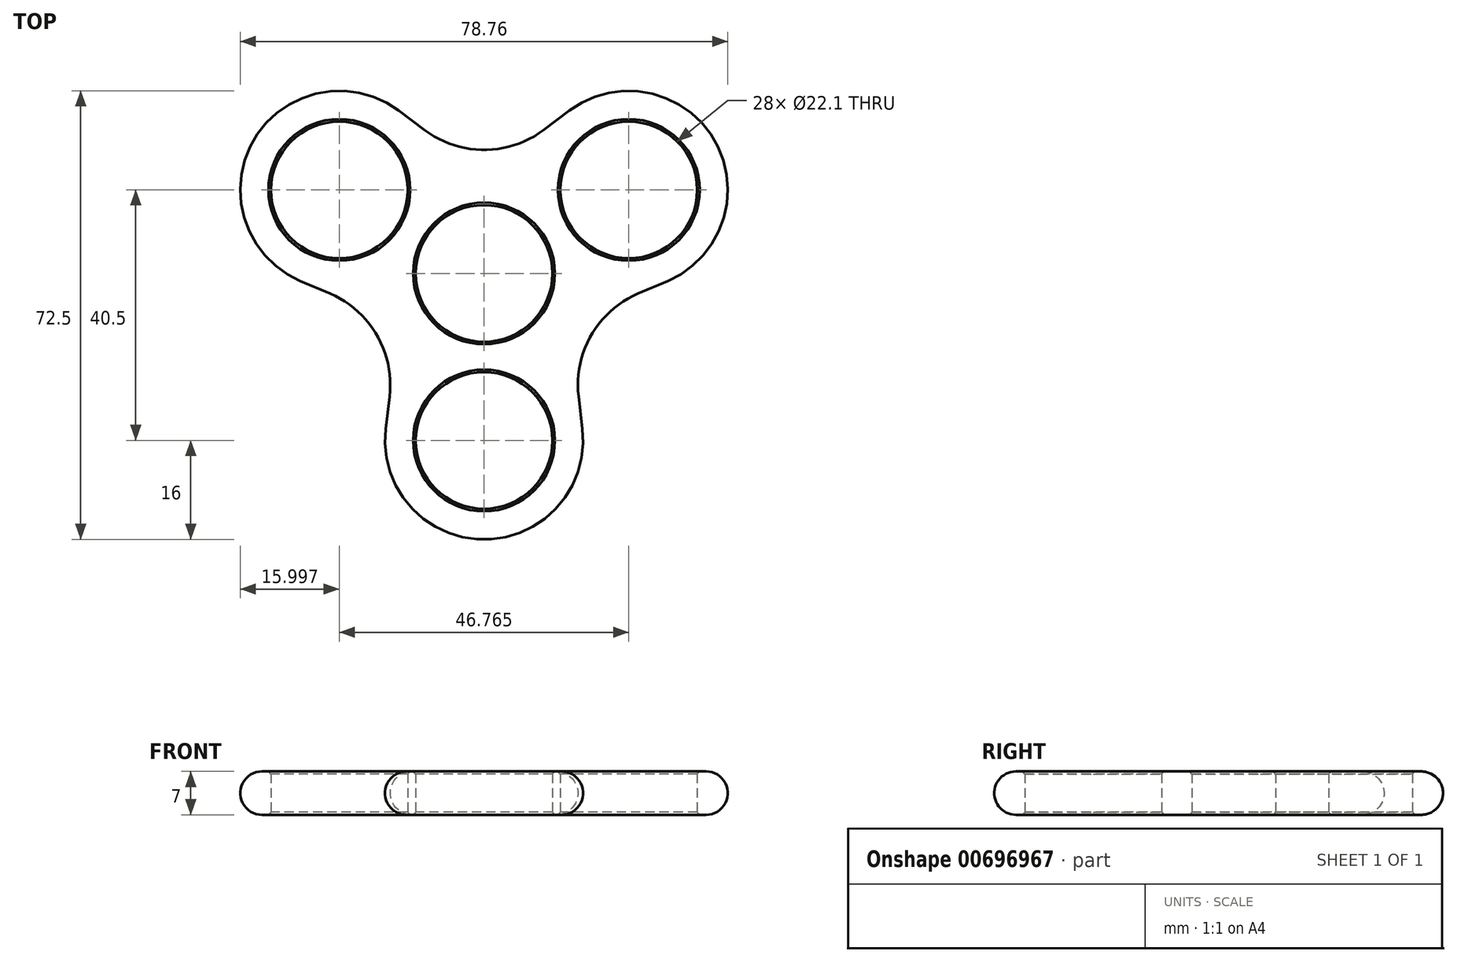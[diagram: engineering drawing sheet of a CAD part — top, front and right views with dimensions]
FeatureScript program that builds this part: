
annotation { "Feature Type Name" : "Feature", "Feature Type Description" : "" }
export const myFeature = defineFeature(function(context is Context, id is Id, definition is map)
    precondition{}
    {
        {
            var Q0;
            Q0=qCreatedBy(makeId("Top.planeOp"),FACE);
            var sketch = newSketch(context, id + "F0", { "sketchPlane" : qUnion([Q0])});
            skLineSegment(sketch, "E0", {"start": v(0, 0) * mm, "end": v(0, -27) * mm, "construction": true});
            skLineSegment(sketch, "E1", {"start": v(0, 0) * mm, "end": v(23.38, 13.5) * mm, "construction": true});
            skLineSegment(sketch, "E2", {"start": v(0, 0) * mm, "end": v(-23.38, 13.5) * mm, "construction": true});
            skCircle(sketch, "E3", {"center": v(-23.38, 13.5) * mm, "radius": 11.05 * mm});
            skCircle(sketch, "E4", {"center": v(23.38, 13.5) * mm, "radius": 11.05 * mm});
            skCircle(sketch, "E5", {"center": v(0, -27) * mm, "radius": 11.05 * mm});
            skCircle(sketch, "E6", {"center": v(0, 0) * mm, "radius": 11.05 * mm});
            skArc(sketch, "E7", {"start": v(-13.8, 26.32) * mm, "mid": v(-37.24, 21.5) * mm, "end": v(-29.7, -1.2) * mm});
            skLineSegment(sketch, "E8", {"start": v(-9.58, 23.16) * mm, "end": v(-13.8, 26.32) * mm});
            skLineSegment(sketch, "E9", {"start": v(9.58, 23.16) * mm, "end": v(13.8, 26.32) * mm});
            skPoint(sketch, "E10.visualSharp", {"position": v(0, 16) * mm});
            skArc(sketch, "E10.filletArc", {"start": v(-9.58, 23.16) * mm, "mid": v(0, 19.97) * mm, "end": v(9.58, 23.16) * mm});
            skLineSegment(sketch, "E11", {"start": v(0, 0) * mm, "end": v(-43.3, -25) * mm, "construction": true});
            skLineSegment(sketch, "E12", {"start": v(0, 0) * mm, "end": v(43.3, -25) * mm, "construction": true});
            skLineSegment(sketch, "E13", {"start": v(15.27, -19.87) * mm, "end": v(15.89, -25.11) * mm});
            skLineSegment(sketch, "E14", {"start": v(-15.27, -19.87) * mm, "end": v(-15.89, -25.11) * mm});
            skLineSegment(sketch, "E15", {"start": v(-24.84, -3.28) * mm, "end": v(-29.7, -1.2) * mm});
            skLineSegment(sketch, "E16", {"start": v(24.84, -3.28) * mm, "end": v(29.7, -1.2) * mm});
            skPoint(sketch, "E17.visualSharp", {"position": v(13.86, -8) * mm});
            skArc(sketch, "E17.filletArc", {"start": v(24.84, -3.28) * mm, "mid": v(17.3, -9.99) * mm, "end": v(15.27, -19.87) * mm});
            skPoint(sketch, "E18.visualSharp", {"position": v(-13.86, -8) * mm});
            skArc(sketch, "E18.filletArc", {"start": v(-15.27, -19.87) * mm, "mid": v(-17.3, -9.99) * mm, "end": v(-24.84, -3.28) * mm});
            skArc(sketch, "E19.trimOffspring", {"start": v(29.7, -1.2) * mm, "mid": v(37.24, 21.5) * mm, "end": v(13.8, 26.32) * mm});
            skArc(sketch, "E20.trimOffspring", {"start": v(-15.89, -25.11) * mm, "mid": v(0, -43) * mm, "end": v(15.89, -25.11) * mm});
            skSolve(sketch);
        }
        {
            var Q0;
            Q0=qSketchRegion(id+"F0",true);
            extrude(context, id + "F1", {"entities" : qUnion([Q0]), "depth" : 7 * mm, "offsetDistance" : 25 * mm});
        }
        {
            var Q0;
            Q0=makeQuery(id+"F1.opExtrude","CAP_EDGE",EDGE,{"disambiguationData":[OSD([sQuery(id+"F0.wireOp",EDGE,"E6")])],"isStart":false});
            var Q1;
            Q1=makeQuery(id+"F1.opExtrude","CAP_EDGE",EDGE,{"disambiguationData":[OSD([sQuery(id+"F0.wireOp",EDGE,"E6")])],"isStart":true});
            var Q2;
            Q2=makeQuery(id+"F1.opExtrude","CAP_EDGE",EDGE,{"disambiguationData":[OSD([sQuery(id+"F0.wireOp",EDGE,"E5")])],"isStart":false});
            var Q3;
            Q3=makeQuery(id+"F1.opExtrude","CAP_EDGE",EDGE,{"disambiguationData":[OSD([sQuery(id+"F0.wireOp",EDGE,"E5")])],"isStart":true});
            var Q4;
            Q4=makeQuery(id+"F1.opExtrude","CAP_EDGE",EDGE,{"disambiguationData":[OSD([sQuery(id+"F0.wireOp",EDGE,"E3")])],"isStart":false});
            var Q5;
            Q5=makeQuery(id+"F1.opExtrude","CAP_EDGE",EDGE,{"disambiguationData":[OSD([sQuery(id+"F0.wireOp",EDGE,"E3")])],"isStart":true});
            var Q6;
            Q6=makeQuery(id+"F1.opExtrude","CAP_EDGE",EDGE,{"disambiguationData":[OSD([sQuery(id+"F0.wireOp",EDGE,"E4")])],"isStart":false});
            var Q7;
            Q7=makeQuery(id+"F1.opExtrude","CAP_EDGE",EDGE,{"disambiguationData":[OSD([sQuery(id+"F0.wireOp",EDGE,"E4")])],"isStart":true});
            chamfer(context, id + "F2", {"entities" : qUnion([Q0, Q1, Q2, Q3, Q4, Q5, Q6, Q7]), "width" : 0.4 * mm, "tangentPropagation" : true});
        }
        {
            var Q0;
            Q0=makeQuery(id+"F1.opExtrude","CAP_EDGE",EDGE,{"disambiguationData":[OSD([sQuery(id+"F0.wireOp",EDGE,"E20.trimOffspring")])],"isStart":false});
            var Q1;
            Q1=makeQuery(id+"F1.opExtrude","CAP_EDGE",EDGE,{"disambiguationData":[OSD([sQuery(id+"F0.wireOp",EDGE,"E20.trimOffspring")])],"isStart":true});
            fillet(context, id + "F3", {"entities" : qUnion([Q0, Q1]), "radius" : 3.5 * mm, "tangentPropagation" : true, "allowEdgeOverflow" : false});
        }
    });
